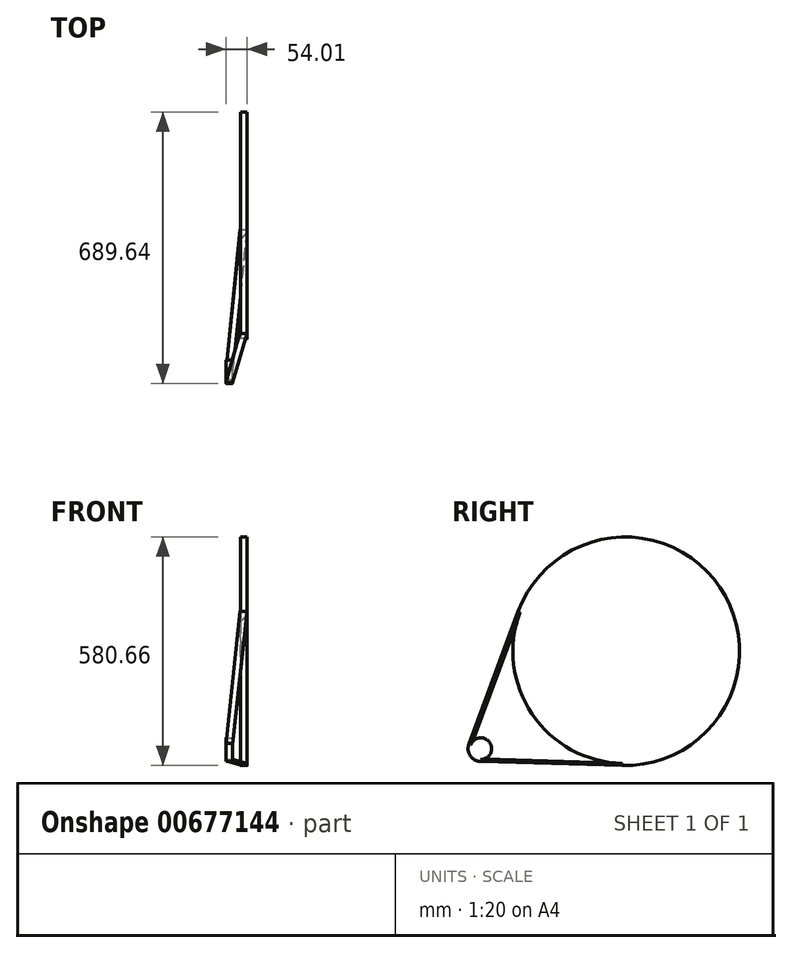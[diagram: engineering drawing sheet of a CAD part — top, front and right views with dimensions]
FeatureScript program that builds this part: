
annotation { "Feature Type Name" : "Feature", "Feature Type Description" : "" }
export const myFeature = defineFeature(function(context is Context, id is Id, definition is map)
    precondition{}
    {
        {
            var Q0;
            Q0=qCreatedBy(makeId("Right.planeOp"),FACE);
            var sketch = newSketch(context, id + "F0", { "sketchPlane" : qUnion([Q0])});
            skCircle(sketch, "E0", {"center": v(0, 0) * mm, "radius": 285.33 * mm});
            skSolve(sketch);
        }
        {
            var Q0;
            Q0=makeQuery(id+"F0.imprint","IMPRINT",FACE,{"disambiguationData":[TD([[makeQuery(id+"F0.imprint","IMPRINT",EDGE,{"derivedFrom":sQuery(id+"F0.wireOp",EDGE,"E0")}),1.0]])]});
            extrude(context, id + "F1", {"entities" : qUnion([Q0]), "depth" : 17.27 * mm, "offsetDistance" : 25.4 * mm, "symmetric" : true});
        }
        {
            var Q0;
            Q0=qCreatedBy(makeId("Front.planeOp"),FACE);
            var sketch = newSketch(context, id + "F2", { "sketchPlane" : qUnion([Q0])});
            skLineSegment(sketch, "E1", {"start": v(-27.87, 0) * mm, "end": v(-8.64, 0) * mm});
            skSolve(sketch);
        }
        {
            var Q0;
            Q0=sQuery(id+"F2.wireOp",VERTEX,"E1.start");
            var Q1;
            Q1=makeQuery(id+"F1.opExtrude","CAP_FACE",FACE,{"disambiguationData":[OSD([sQuery(id+"F0.wireOp",EDGE,"E0")])],"isStart":true});
            cPlane(context, id + "F3", {"entities" : qUnion([Q0, Q1]), "cplaneType" : CPlaneType.PLANE_POINT, "offset" : 25.4 * mm, "width" : 152.4 * mm, "height" : 152.4 * mm});
        }
        {
            var Q0;
            Q0=qCreatedBy(id+"F3.planeOp",FACE);
            var sketch = newSketch(context, id + "F4", { "sketchPlane" : qUnion([Q0])});
            skLineSegment(sketch, "E2", {"start": v(0, 0) * mm, "end": v(366.81, 0) * mm, "construction": true});
            skLineSegment(sketch, "E3", {"start": v(366.81, 0) * mm, "end": v(366.81, -247.54) * mm, "construction": true});
            skCircle(sketch, "E4", {"center": v(366.81, -247.54) * mm, "radius": 27.5 * mm});
            skSolve(sketch);
        }
        {
            var Q0;
            Q0=makeQuery(id+"F4.imprint","IMPRINT",FACE,{"disambiguationData":[TD([[makeQuery(id+"F4.imprint","IMPRINT",EDGE,{"derivedFrom":sQuery(id+"F4.wireOp",EDGE,"E4")}),1.0]])]});
            extrude(context, id + "F5", {"entities" : qUnion([Q0]), "depth" : 17.27 * mm, "offsetDistance" : 25.4 * mm});
        }
        {
            var Q0;
            Q0=makeQuery(id+"F1.opExtrude","CAP_FACE",FACE,{"disambiguationData":[OSD([sQuery(id+"F0.wireOp",EDGE,"E0")])],"isStart":false});
            var sketch = newSketch(context, id + "F6", { "sketchPlane" : qUnion([Q0])});
            skLineSegment(sketch, "E5", {"start": v(-172.98, 354.12) * mm, "end": v(-474.61, -459.1) * mm});
            skLineSegment(sketch, "E6", {"start": v(-550.6, -269.85) * mm, "end": v(543.62, -300.85) * mm});
            skPoint(sketch, "E7", {"position": v(-8.08, -285.22) * mm});
            skPoint(sketch, "E8", {"position": v(-267.52, 99.23) * mm});
            skArc(sketch, "E9", {"start": v(-8.08, -285.22) * mm, "mid": v(236.51, 159.61) * mm, "end": v(-267.52, 99.23) * mm});
            skArc(sketch, "E10.0", {"start": v(-8.22, -290.21) * mm, "mid": v(240.66, 162.4) * mm, "end": v(-272.2, 100.97) * mm});
            skLineSegment(sketch, "E11", {"start": v(-272.2, 100.97) * mm, "end": v(-267.52, 99.23) * mm});
            skLineSegment(sketch, "E12", {"start": v(-8.22, -290.21) * mm, "end": v(-8.08, -285.22) * mm});
            skLineSegment(sketch, "E13", {"start": v(0, 0) * mm, "end": v(-405.94, -273.94) * mm, "construction": true});
            skLineSegment(sketch, "E14", {"start": v(0, 0) * mm, "end": v(236.51, 159.61) * mm, "construction": true});
            skPoint(sketch, "E15", {"position": v(-392.6, -237.98) * mm});
            skPoint(sketch, "E16", {"position": v(-367.6, -275.03) * mm});
            skSolve(sketch);
        }
        {
            var Q0;
            Q0=makeQuery(id+"F5.opExtrude","CAP_FACE",FACE,{"disambiguationData":[OSD([sQuery(id+"F4.wireOp",EDGE,"E4")])],"isStart":false});
            var sketch = newSketch(context, id + "F7", { "sketchPlane" : qUnion([Q0])});
            skPoint(sketch, "E17", {"position": v(389.6, -262.93) * mm});
            skSolve(sketch);
        }
        {
            var Q0;
            Q0=makeQuery(id+"F5.opExtrude","CAP_FACE",FACE,{"disambiguationData":[OSD([sQuery(id+"F4.wireOp",EDGE,"E4")])],"isStart":true});
            var sketch = newSketch(context, id + "F8", { "sketchPlane" : qUnion([Q0])});
            skPoint(sketch, "E18", {"position": v(-389.6, -262.93) * mm});
            skPoint(sketch, "E19", {"position": v(-392.6, -237.98) * mm});
            skPoint(sketch, "E20", {"position": v(-367.6, -275.03) * mm});
            skArc(sketch, "E21", {"start": v(-392.6, -237.98) * mm, "mid": v(-389.6, -262.93) * mm, "end": v(-367.6, -275.03) * mm});
            skSolve(sketch);
        }
        {
            var Q0;
            {var subQ0=sQuery(id+"F6.wireOp",EDGE,"E9");Q0=makeQuery(id+"F6.imprint","IMPRINT",FACE,{"disambiguationData":[TD([[makeQuery(id+"F6.imprint","IMPRINT",EDGE,{"derivedFrom":subQ0}),-1.0]])]});}
            var Q1;
            {var subQ0=sQuery(id+"F6.wireOp",EDGE,"E11");Q1=makeQuery(id+"F6.imprint","IMPRINT",FACE,{"disambiguationData":[TD([[makeQuery(id+"F6.imprint","IMPRINT",EDGE,{"derivedFrom":subQ0}),1.0]])]});}
            var Q2;
            {var subQ0=sQuery(id+"F6.wireOp",EDGE,"E12");Q2=makeQuery(id+"F6.imprint","IMPRINT",FACE,{"disambiguationData":[TD([[makeQuery(id+"F6.imprint","IMPRINT",EDGE,{"derivedFrom":subQ0}),-1.0]])]});}
            var Q3;
            Q3=makeQuery(id+"F1.opExtrude","CAP_FACE",FACE,{"disambiguationData":[OSD([sQuery(id+"F0.wireOp",EDGE,"E0")])],"isStart":true});
            extrude(context, id + "F9", {"entities" : qUnion([Q0, Q1, Q2]), "endBound" : BoundingType.UP_TO_SURFACE, "oppositeDirection" : true, "depth" : 25.4 * mm, "endBoundEntityFace" : qUnion([Q3]), "offsetDistance" : 25.4 * mm});
        }
        {
            var Q0;
            Q0=sQuery(id+"F6.wireOp",VERTEX,"E8");
            var Q1;
            Q1=sQuery(id+"F8.wireOp",VERTEX,"E19");
            var Q2;
            Q2=sQuery(id+"F8.wireOp",VERTEX,"E20");
            cPlane(context, id + "F10", {"entities" : qUnion([Q0, Q1, Q2]), "cplaneType" : CPlaneType.THREE_POINT, "offset" : 25.4 * mm, "width" : 152.4 * mm, "height" : 152.4 * mm});
        }
        {
            var Q0;
            Q0=qCreatedBy(id+"F10.planeOp",FACE);
            var sketch = newSketch(context, id + "F11", { "sketchPlane" : qUnion([Q0])});
            skLineSegment(sketch, "E22", {"start": v(265.93, 99.59) * mm, "end": v(391.67, -239.34) * mm});
            skLineSegment(sketch, "E23", {"start": v(366.53, -276.3) * mm, "end": v(5.11, -283.92) * mm});
            skLineSegment(sketch, "E24", {"start": v(5.11, -283.92) * mm, "end": v(5.22, -288.9) * mm});
            skLineSegment(sketch, "E25", {"start": v(5.22, -288.9) * mm, "end": v(366.64, -281.3) * mm});
            skLineSegment(sketch, "E26", {"start": v(366.64, -281.3) * mm, "end": v(366.53, -276.3) * mm});
            skLineSegment(sketch, "E27", {"start": v(391.67, -239.34) * mm, "end": v(396.36, -237.6) * mm});
            skLineSegment(sketch, "E28", {"start": v(396.36, -237.6) * mm, "end": v(270.6, 101.32) * mm});
            skLineSegment(sketch, "E29", {"start": v(270.6, 101.32) * mm, "end": v(265.93, 99.59) * mm});
            skSolve(sketch);
        }
        {
            var Q0;
            Q0=makeQuery(id+"F11.imprint","IMPRINT",FACE,{"disambiguationData":[TD([[makeQuery(id+"F11.imprint","IMPRINT",EDGE,{"derivedFrom":sQuery(id+"F11.wireOp",EDGE,"E23")}),1.0]])]});
            var Q1;
            Q1=makeQuery(id+"F11.imprint","IMPRINT",FACE,{"disambiguationData":[TD([[makeQuery(id+"F11.imprint","IMPRINT",EDGE,{"derivedFrom":sQuery(id+"F11.wireOp",EDGE,"E22")}),1.0]])]});
            extrude(context, id + "F12", {"entities" : qUnion([Q0, Q1]), "operationType" : NewBodyOperationType.ADD, "depth" : 17.27 * mm, "offsetDistance" : 25.4 * mm});
        }
        {
            var Q0;
            {var subQ0=sQuery(id+"F8.wireOp",EDGE,"E21");Q0=makeQuery(id+"F8.imprint","IMPRINT",FACE,{"disambiguationData":[TD([[makeQuery(id+"F8.imprint","IMPRINT",EDGE,{"derivedFrom":subQ0}),-1.0]])]});}
            var sketch = newSketch(context, id + "F13", { "sketchPlane" : qUnion([Q0])});
            skArc(sketch, "E30", {"start": v(-391.96, -236.42) * mm, "mid": v(-388.78, -264.09) * mm, "end": v(-363.07, -274.79) * mm});
            skPoint(sketch, "E31", {"position": v(-393.15, -235.9) * mm});
            skLineSegment(sketch, "E32", {"start": v(-366.81, -247.54) * mm, "end": v(-391.96, -236.42) * mm, "construction": true});
            skArc(sketch, "E33.0", {"start": v(-396.21, -233.7) * mm, "mid": v(-393, -266.78) * mm, "end": v(-362.39, -279.74) * mm});
            skLineSegment(sketch, "E34", {"start": v(-396.21, -233.7) * mm, "end": v(-391.96, -236.42) * mm});
            skLineSegment(sketch, "E35", {"start": v(-362.39, -279.74) * mm, "end": v(-363.07, -274.79) * mm});
            skSolve(sketch);
        }
        {
            var Q0;
            Q0=makeQuery(id+"F13.imprint","IMPRINT",FACE,{"disambiguationData":[TD([[makeQuery(id+"F13.imprint","IMPRINT",EDGE,{"derivedFrom":sQuery(id+"F13.wireOp",EDGE,"E33.0")}),1.0]])]});
            extrude(context, id + "F14", {"entities" : qUnion([Q0]), "operationType" : NewBodyOperationType.ADD, "oppositeDirection" : true, "depth" : 17.27 * mm, "offsetDistance" : 25.4 * mm});
        }
    });
